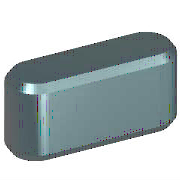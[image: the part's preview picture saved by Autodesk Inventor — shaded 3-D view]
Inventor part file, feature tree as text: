
AUTODESK INVENTOR PART (.ipt)
format: ipt  version: 2015 (Build 190159000, 159)  size: 137,216 bytes
history: native  units: mm (DEFAULTED — no unit token found)
features: plane x3, extrude x1
ambient origin geometry x8: Origin, YZ Plane, XZ Plane, XY Plane, X Axis, Y Axis, Z Axis, Center Point
bodies: Solid1 (feature_tree)
feature tree (4):
  plane  "Work Plane1"
  plane  "Work Plane2"
  extrude  "轴承体1"  Depth=4.0mm
  plane  "Work Plane3"
